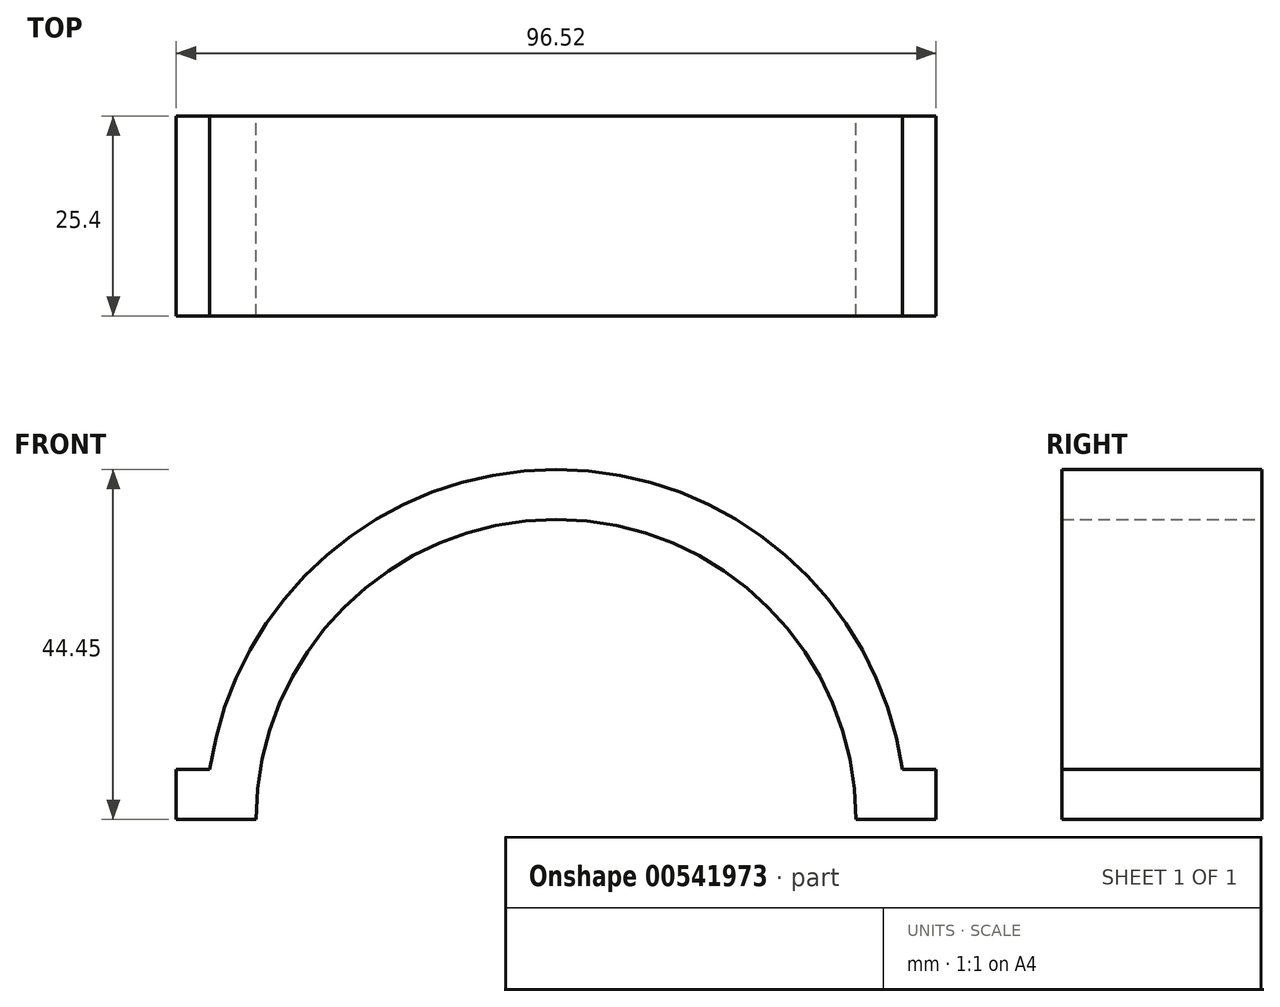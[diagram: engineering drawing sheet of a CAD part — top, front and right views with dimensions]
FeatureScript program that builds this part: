
annotation { "Feature Type Name" : "Feature", "Feature Type Description" : "" }
export const myFeature = defineFeature(function(context is Context, id is Id, definition is map)
    precondition{}
    {
        {
            var Q0;
            Q0=qCreatedBy(makeId("Front.planeOp"),FACE);
            var sketch = newSketch(context, id + "F0", { "sketchPlane" : qUnion([Q0])});
            skArc(sketch, "E0", {"start": v(38.1, 0) * mm, "mid": v(0, 38.1) * mm, "end": v(-38.1, 0) * mm});
            skLineSegment(sketch, "E1", {"start": v(38.1, 0) * mm, "end": v(48.26, 0) * mm});
            skLineSegment(sketch, "E2", {"start": v(-38.1, 0) * mm, "end": v(-48.26, 0) * mm});
            skLineSegment(sketch, "E3.0", {"start": v(-44, 6.35) * mm, "end": v(-48.26, 6.35) * mm});
            skArc(sketch, "E3.1", {"start": v(44, 6.35) * mm, "mid": v(0, 44.45) * mm, "end": v(-44, 6.35) * mm});
            skLineSegment(sketch, "E3.2", {"start": v(44, 6.35) * mm, "end": v(48.26, 6.35) * mm});
            skLineSegment(sketch, "E4", {"start": v(48.26, 0) * mm, "end": v(48.26, 6.35) * mm});
            skLineSegment(sketch, "E5", {"start": v(-48.26, 6.35) * mm, "end": v(-48.26, 0) * mm});
            skSolve(sketch);
        }
        {
            var Q0;
            Q0 = qSketchRegion(id + "F0", true);
            extrude(context, id + "F1", {"entities" : qUnion([Q0]), "depth" : 25.4 * mm, "offsetDistance" : 25.4 * mm});
        }
    });
